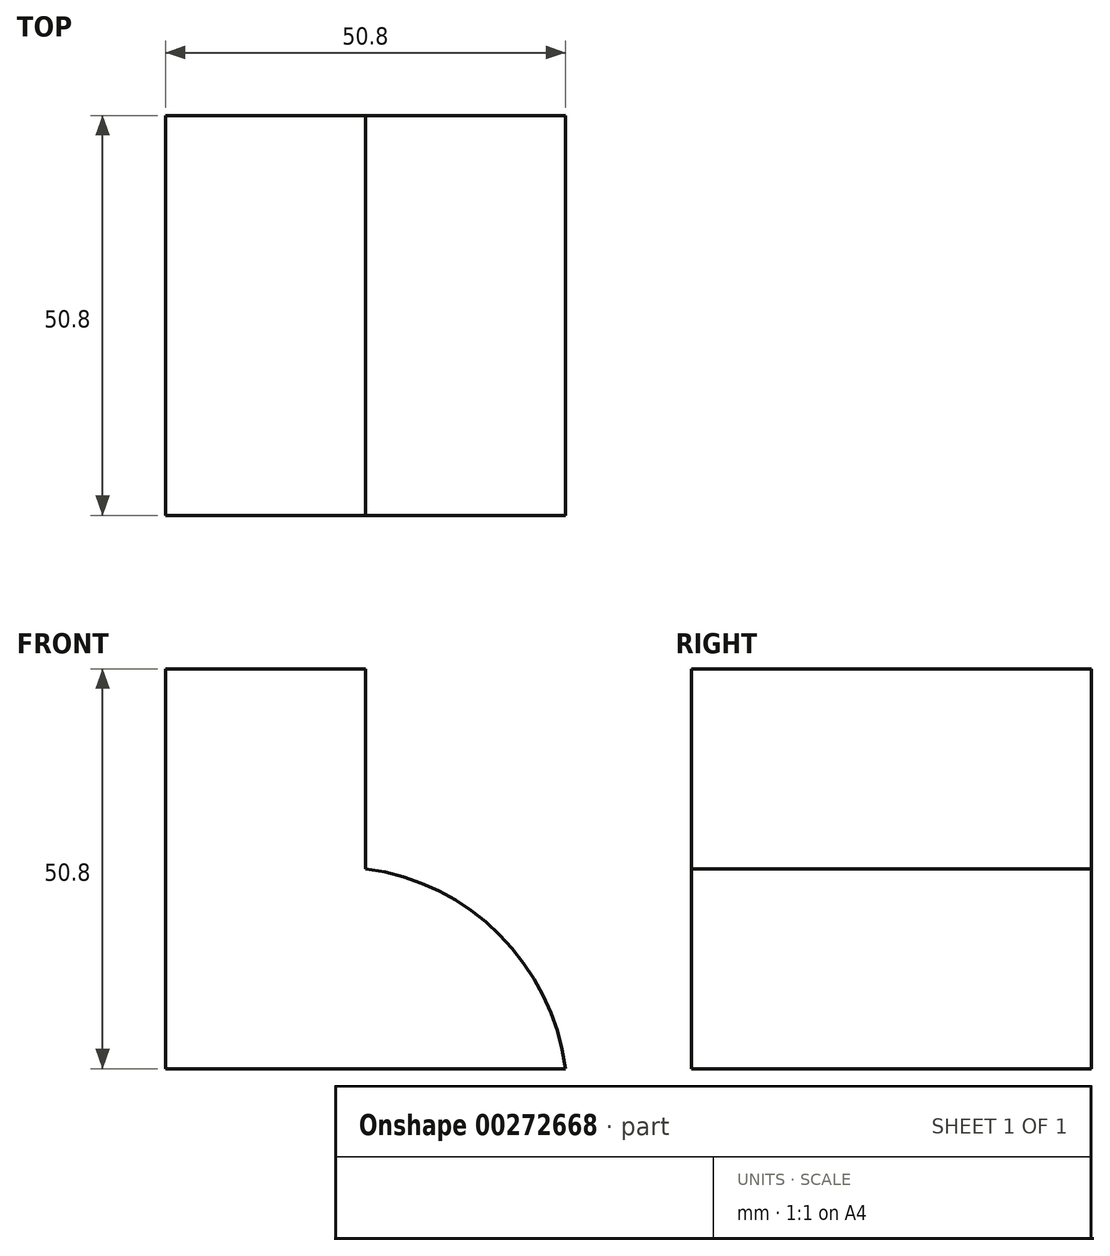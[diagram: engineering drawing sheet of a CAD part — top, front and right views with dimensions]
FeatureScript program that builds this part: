
annotation { "Feature Type Name" : "Feature", "Feature Type Description" : "" }
export const myFeature = defineFeature(function(context is Context, id is Id, definition is map)
    precondition{}
    {
        {
            var Q0;
            Q0=qCreatedBy(makeId("Front.planeOp"),FACE);
            var sketch = newSketch(context, id + "F0", { "sketchPlane" : qUnion([Q0])});
            skLineSegment(sketch, "E0", {"start": v(0, 0) * mm, "end": v(-50.8, 0) * mm});
            skLineSegment(sketch, "E1", {"start": v(-50.8, 0) * mm, "end": v(-50.8, 50.8) * mm});
            skLineSegment(sketch, "E2", {"start": v(-50.8, 50.8) * mm, "end": v(-25.4, 50.8) * mm});
            skLineSegment(sketch, "E3", {"start": v(-25.4, 50.8) * mm, "end": v(-25.4, 25.4) * mm});
            skArc(sketch, "E4", {"start": v(0, 0) * mm, "mid": v(-8.38, 17.02) * mm, "end": v(-25.4, 25.4) * mm});
            skSolve(sketch);
        }
        {
            var Q0;
            Q0=makeQuery(id+"F0.imprint","IMPRINT",FACE,{"disambiguationData":[TD([[makeQuery(id+"F0.imprint","IMPRINT",EDGE,{"derivedFrom":sQuery(id+"F0.wireOp",EDGE,"E0")}),-1.0]])]});
            extrude(context, id + "F1", {"entities" : qUnion([Q0]), "depth" : 50.8 * mm});
        }
    });
